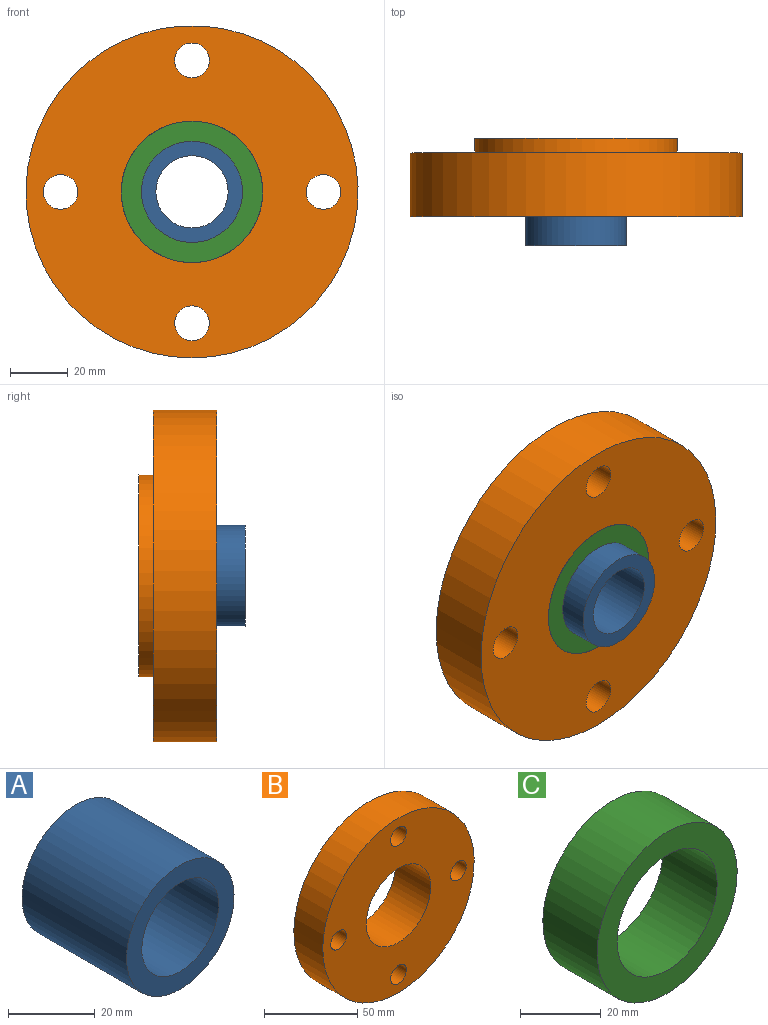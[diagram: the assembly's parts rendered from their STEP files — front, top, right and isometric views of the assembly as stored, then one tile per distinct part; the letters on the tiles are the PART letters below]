
ASSEMBLY  parts=3 mates=2
PART A: 4 faces, bbox 35x34x35 mm
  f0: cylinder r=12.5mm len=34mm, axis (0,1,0), area 2670.4mm2, adj f2,f3
  f1: cylinder r=17.5mm len=35mm, axis (0,1,0), area 3738.5mm2, adj f2,f3
  f2: plane 35x35mm, normal (0,-1,0), area 471.2mm2, adj f0,f1
  f3: plane 35x35mm, normal (0,1,0), area 471.2mm2, adj f0,f1
PART B: 10 faces, bbox 115x27x115 mm
  f0: cylinder r=57.5mm len=115mm, axis (0,1,0), area 7948.2mm2, adj f6,f7
  f1: cylinder r=6mm len=22mm, axis (0,1,0), area 829.4mm2, adj f6,f7
  f2: cylinder r=6mm len=22mm, axis (0,1,0), area 829.4mm2, adj f6,f7
  f3: cylinder r=6mm len=22mm, axis (0,1,0), area 829.4mm2, adj f6,f7
  f4: cylinder r=6mm len=22mm, axis (0,1,0), area 829.4mm2, adj f6,f7
  f5: cylinder r=24.5mm len=49mm, axis (0,1,0), area 4156.3mm2, adj f6,f9
  f6: plane 115x115mm, normal (0,-1,0), area 8048.8mm2, adj f0,f1,f2,f3,f4,f5
  f7: plane 115x115mm, normal (0,1,0), area 6086.1mm2, adj f0,f1,f2,f3,f4,f8
  f8: cylinder r=35mm len=70mm, axis (0,-1,0), area 1099.6mm2, adj f7,f9
  f9: plane 70x70mm, normal (0,1,0), area 1962.7mm2, adj f5,f8
PART C: 4 faces, bbox 49x19x49 mm
  f0: cylinder r=17.5mm len=35mm, axis (0,1,0), area 2089.2mm2, adj f2,f3
  f1: cylinder r=24.5mm len=49mm, axis (0,1,0), area 2924.8mm2, adj f2,f3
  f2: plane 49x49mm, normal (0,-1,0), area 923.6mm2, adj f0,f1
  f3: plane 49x49mm, normal (0,1,0), area 923.6mm2, adj f0,f1
PLACE A rot(axis=(-1,0,0),180deg) t=(58.9,-28.19,240.65)mm
PLACE B t=(-33.49,3.81,5.94)mm
PLACE C rot(axis=(1,0,0),180deg) t=(5.71,-18.19,171.18)mm
MATE fastened A.f0 <-> C.f0  axis (0,1,0) through (-114.67,5.81,171.18)mm
MATE fastened C.f0 <-> B.f0  axis (0,-1,0) through (-114.67,-18.19,171.18)mm
